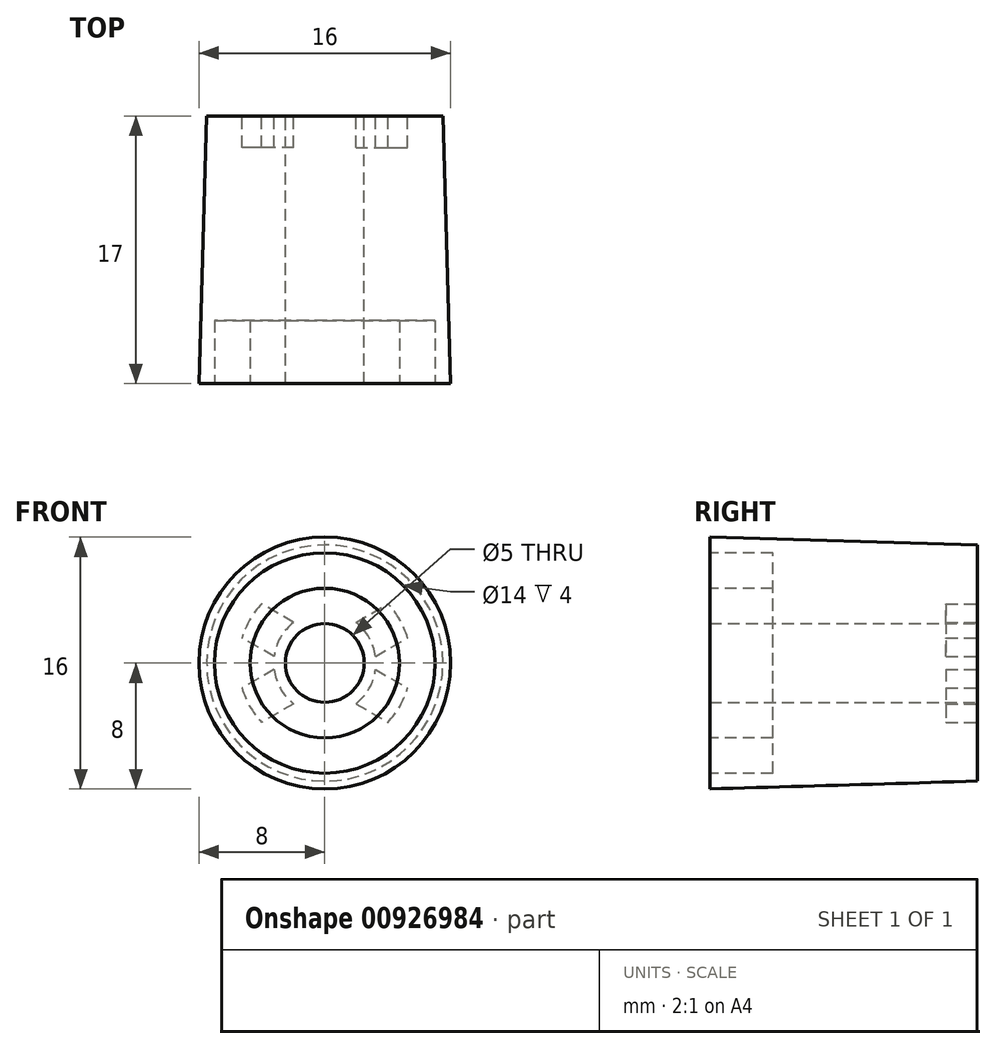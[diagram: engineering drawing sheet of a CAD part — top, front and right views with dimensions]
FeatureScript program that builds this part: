
annotation { "Feature Type Name" : "Feature", "Feature Type Description" : "" }
export const myFeature = defineFeature(function(context is Context, id is Id, definition is map)
    precondition{}
    {
        {
            var Q0;
            Q0=qCreatedBy(makeId("Front.planeOp"),FACE);
            var sketch = newSketch(context, id + "F0", { "sketchPlane" : qUnion([Q0])});
            skCircle(sketch, "E0", {"center": v(0, 0) * mm, "radius": 8 * mm});
            skCircle(sketch, "E1", {"center": v(0, 0) * mm, "radius": 2.5 * mm});
            skSolve(sketch);
        }
        {
            var Q0;
            Q0=makeQuery(id+"F0.imprint","IMPRINT",FACE,{"disambiguationData":[TD([[makeQuery(id+"F0.imprint","IMPRINT",EDGE,{"derivedFrom":sQuery(id+"F0.wireOp",EDGE,"E0")}),1.0]])]});
            extrude(context, id + "F1", {"entities" : qUnion([Q0]), "depth" : 17 * mm, "offsetDistance" : 25 * mm});
        }
        {
            var Q0;
            Q0=makeQuery(id+"F1.opExtrude","CAP_FACE",FACE,{"disambiguationData":[OSD([sQuery(id+"F0.wireOp",EDGE,"E0"),sQuery(id+"F0.wireOp",EDGE,"E1")])],"isStart":false});
            var sketch = newSketch(context, id + "F2", { "sketchPlane" : qUnion([Q0])});
            skCircle(sketch, "E2.0", {"center": v(0, 0) * mm, "radius": 8 * mm});
            skCircle(sketch, "E3.0", {"center": v(0, 0) * mm, "radius": 2.5 * mm});
            skCircle(sketch, "E4", {"center": v(0, 0) * mm, "radius": 7 * mm});
            skCircle(sketch, "E5", {"center": v(0, 0) * mm, "radius": 4.75 * mm});
            skSolve(sketch);
        }
        {
            var Q0;
            Q0=makeQuery(id+"F2.imprint","IMPRINT",FACE,{"disambiguationData":[TD([[makeQuery(id+"F2.imprint","IMPRINT",EDGE,{"derivedFrom":sQuery(id+"F2.wireOp",EDGE,"E4")}),1.0]])]});
            extrude(context, id + "F3", {"entities" : qUnion([Q0]), "operationType" : NewBodyOperationType.REMOVE, "oppositeDirection" : true, "depth" : 4 * mm, "offsetDistance" : 25 * mm});
        }
        {
            var Q0;
            Q0=makeQuery(id+"F1.opExtrude","CAP_FACE",FACE,{"disambiguationData":[OSD([sQuery(id+"F0.wireOp",EDGE,"E0"),sQuery(id+"F0.wireOp",EDGE,"E1")])],"isStart":true});
            var sketch = newSketch(context, id + "F4", { "sketchPlane" : qUnion([Q0])});
            skArc(sketch, "E6", {"start": v(-1.97, 2.58) * mm, "mid": v(-2.81, 1.62) * mm, "end": v(-3.22, 0.42) * mm});
            skArc(sketch, "E7", {"start": v(-4.01, 3.76) * mm, "mid": v(-4.76, 2.75) * mm, "end": v(-5.26, 1.6) * mm});
            skLineSegment(sketch, "E8", {"start": v(-3.22, 0.42) * mm, "end": v(-5.26, 1.6) * mm});
            skLineSegment(sketch, "E9", {"start": v(-1.97, 2.58) * mm, "end": v(-4.01, 3.76) * mm});
            skLineSegment(sketch, "E10", {"start": v(0, 0) * mm, "end": v(-6.93, 4) * mm, "construction": true});
            skLineSegment(sketch, "E11", {"start": v(0, 0) * mm, "end": v(-8, 0) * mm, "construction": true});
            skArc(sketch, "E12.1.0", {"start": v(-5.26, -1.6) * mm, "mid": v(-4.76, -2.75) * mm, "end": v(-4.01, -3.76) * mm});
            skLineSegment(sketch, "E12.1.1", {"start": v(-3.22, -0.42) * mm, "end": v(-5.26, -1.6) * mm});
            skArc(sketch, "E12.1.2", {"start": v(-3.22, -0.42) * mm, "mid": v(-2.81, -1.62) * mm, "end": v(-1.97, -2.58) * mm});
            skLineSegment(sketch, "E12.1.3", {"start": v(-1.97, -2.58) * mm, "end": v(-4.01, -3.76) * mm});
            skArc(sketch, "E12.2.0", {"start": v(-1.25, -5.36) * mm, "mid": v(0, -5.5) * mm, "end": v(1.25, -5.36) * mm});
            skLineSegment(sketch, "E12.2.1", {"start": v(-1.25, -3) * mm, "end": v(-1.25, -5.36) * mm});
            skArc(sketch, "E12.2.2", {"start": v(-1.25, -3) * mm, "mid": v(0, -3.25) * mm, "end": v(1.25, -3) * mm});
            skLineSegment(sketch, "E12.2.3", {"start": v(1.25, -3) * mm, "end": v(1.25, -5.36) * mm});
            skArc(sketch, "E12.3.0", {"start": v(4.01, -3.76) * mm, "mid": v(4.76, -2.75) * mm, "end": v(5.26, -1.6) * mm});
            skLineSegment(sketch, "E12.3.1", {"start": v(1.97, -2.58) * mm, "end": v(4.01, -3.76) * mm});
            skArc(sketch, "E12.3.2", {"start": v(1.97, -2.58) * mm, "mid": v(2.81, -1.62) * mm, "end": v(3.22, -0.42) * mm});
            skLineSegment(sketch, "E12.3.3", {"start": v(3.22, -0.42) * mm, "end": v(5.26, -1.6) * mm});
            skArc(sketch, "E13.3.4.0", {"start": v(5.26, 1.6) * mm, "mid": v(4.76, 2.75) * mm, "end": v(4.01, 3.76) * mm});
            skLineSegment(sketch, "E13.4.4.0", {"start": v(3.22, 0.42) * mm, "end": v(5.26, 1.6) * mm});
            skArc(sketch, "E13.7.4.0", {"start": v(3.22, 0.42) * mm, "mid": v(2.81, 1.62) * mm, "end": v(1.97, 2.58) * mm});
            skLineSegment(sketch, "E13.11.4.0", {"start": v(1.97, 2.58) * mm, "end": v(4.01, 3.76) * mm});
            skArc(sketch, "E13.3.5.0", {"start": v(1.25, 5.36) * mm, "mid": v(0, 5.5) * mm, "end": v(-1.25, 5.36) * mm});
            skLineSegment(sketch, "E13.4.5.0", {"start": v(1.25, 3) * mm, "end": v(1.25, 5.36) * mm});
            skArc(sketch, "E13.7.5.0", {"start": v(1.25, 3) * mm, "mid": v(0, 3.25) * mm, "end": v(-1.25, 3) * mm});
            skLineSegment(sketch, "E13.11.5.0", {"start": v(-1.25, 3) * mm, "end": v(-1.25, 5.36) * mm});
            skSolve(sketch);
        }
        {
            var Q0;
            Q0=makeQuery(id+"F4.imprint","IMPRINT",FACE,{"disambiguationData":[TD([[makeQuery(id+"F4.imprint","IMPRINT",EDGE,{"derivedFrom":sQuery(id+"F4.wireOp",EDGE,"E6")}),-1.0]])]});
            var Q1;
            Q1=makeQuery(id+"F4.imprint","IMPRINT",FACE,{"disambiguationData":[TD([[makeQuery(id+"F4.imprint","IMPRINT",EDGE,{"derivedFrom":sQuery(id+"F4.wireOp",EDGE,"E12.1.0")}),1.0]])]});
            var Q2;
            Q2=makeQuery(id+"F4.imprint","IMPRINT",FACE,{"disambiguationData":[TD([[makeQuery(id+"F4.imprint","IMPRINT",EDGE,{"derivedFrom":sQuery(id+"F4.wireOp",EDGE,"E12.3.0")}),1.0]])]});
            var Q3;
            Q3=makeQuery(id+"F4.imprint","IMPRINT",FACE,{"disambiguationData":[TD([[makeQuery(id+"F4.imprint","IMPRINT",EDGE,{"derivedFrom":sQuery(id+"F4.wireOp",EDGE,"E13.3.4.0")}),1.0]])]});
            extrude(context, id + "F5", {"entities" : qUnion([Q0, Q1, Q2, Q3]), "operationType" : NewBodyOperationType.REMOVE, "oppositeDirection" : true, "depth" : 2 * mm, "offsetDistance" : 25 * mm});
        }
        {
            var Q0;
            Q0=qCreatedBy(makeId("Right.planeOp"),FACE);
            var sketch = newSketch(context, id + "F6", { "sketchPlane" : qUnion([Q0])});
            skLineSegment(sketch, "E14", {"start": v(0, 0) * mm, "end": v(-7.36, 0) * mm, "construction": true});
            skLineSegment(sketch, "E15", {"start": v(-17, 8) * mm, "end": v(0, 7.5) * mm});
            skLineSegment(sketch, "E16", {"start": v(0, 7.5) * mm, "end": v(0, -7.5) * mm});
            skLineSegment(sketch, "E17", {"start": v(0, -7.5) * mm, "end": v(-17, -8) * mm});
            skLineSegment(sketch, "E18", {"start": v(-17, -8) * mm, "end": v(-17, 8) * mm});
            skLineSegment(sketch, "E19", {"start": v(-17, 8) * mm, "end": v(0, 8) * mm});
            skLineSegment(sketch, "E20", {"start": v(0, 8) * mm, "end": v(0, 7.5) * mm});
            skSolve(sketch);
        }
        {
            var Q0;
            Q0=makeQuery(id+"F6.imprint","IMPRINT",FACE,{"disambiguationData":[TD([[makeQuery(id+"F6.imprint","IMPRINT",EDGE,{"derivedFrom":sQuery(id+"F6.wireOp",EDGE,"E15")}),1.0]])]});
            var Q1;
            Q1=sQuery(id+"F6.wireOp",EDGE,"E14");
            revolve(context, id + "F7", {"operationType" : NewBodyOperationType.REMOVE, "surfaceOperationType" : NewSurfaceOperationType.NEW, "entities" : qUnion([Q0]), "axis" : qUnion([Q1]), "revolveType" : RevolveType.FULL, "oppositeDirection" : true});
        }
    });
